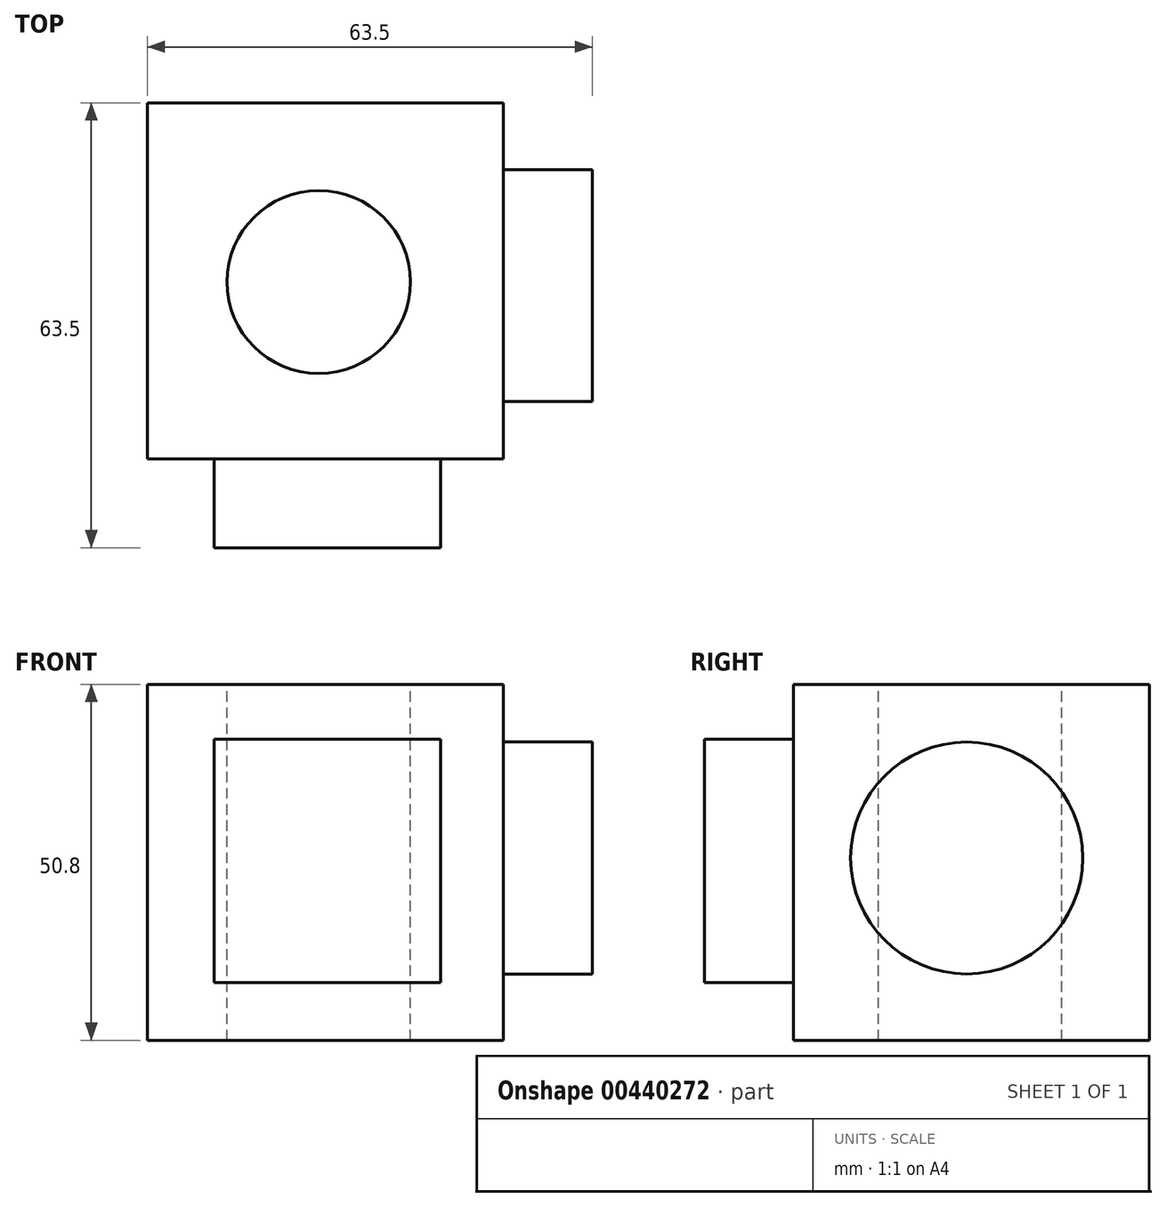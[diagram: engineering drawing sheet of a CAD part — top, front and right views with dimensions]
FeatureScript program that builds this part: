
annotation { "Feature Type Name" : "Feature", "Feature Type Description" : "" }
export const myFeature = defineFeature(function(context is Context, id is Id, definition is map)
    precondition{}
    {
        {
            var Q0;
            Q0=qCreatedBy(makeId("Front.planeOp"),FACE);
            var sketch = newSketch(context, id + "F0", { "sketchPlane" : qUnion([Q0])});
            skLineSegment(sketch, "E0.bottom", {"start": v(0, 0) * mm, "end": v(-50.8, 0) * mm});
            skLineSegment(sketch, "E0.top", {"start": v(0, 50.8) * mm, "end": v(-50.8, 50.8) * mm});
            skLineSegment(sketch, "E0.left", {"start": v(0, 0) * mm, "end": v(0, 50.8) * mm});
            skLineSegment(sketch, "E0.right", {"start": v(-50.8, 0) * mm, "end": v(-50.8, 50.8) * mm});
            skSolve(sketch);
        }
        {
            var Q0;
            Q0 = qSketchRegion(id + "F0", true);
            extrude(context, id + "F1", {"entities" : qUnion([Q0]), "depth" : 50.8 * mm});
        }
        {
            var Q0;
            Q0=makeQuery(id+"F1.opExtrude","SWEPT_FACE",FACE,{"disambiguationData":[OSD([sQuery(id+"F0.wireOp",EDGE,"E0.top")])]});
            var sketch = newSketch(context, id + "F2", { "sketchPlane" : qUnion([Q0])});
            skCircle(sketch, "E1", {"center": v(-26.35, -25.59) * mm, "radius": 13.07 * mm});
            skSolve(sketch);
        }
        {
            var Q0;
            Q0=makeQuery(id+"F2.imprint","IMPRINT",FACE,{"disambiguationData":[TD([[makeQuery(id+"F2.imprint","IMPRINT",EDGE,{"derivedFrom":sQuery(id+"F2.wireOp",EDGE,"E1")}),1.0]])]});
            extrude(context, id + "F3", {"entities" : qUnion([Q0]), "operationType" : NewBodyOperationType.REMOVE, "oppositeDirection" : true, "depth" : 50.8 * mm});
        }
        {
            var Q0;
            Q0=makeQuery(id+"F1.opExtrude","SWEPT_FACE",FACE,{"disambiguationData":[OSD([sQuery(id+"F0.wireOp",EDGE,"E0.left")])]});
            var sketch = newSketch(context, id + "F4", { "sketchPlane" : qUnion([Q0])});
            skCircle(sketch, "E2", {"center": v(-26.09, 26) * mm, "radius": 16.56 * mm});
            skSolve(sketch);
        }
        {
            var Q0;
            Q0 = qSketchRegion(id + "F4", true);
            extrude(context, id + "F5", {"entities" : qUnion([Q0]), "operationType" : NewBodyOperationType.ADD, "depth" : 12.7 * mm});
        }
        {
            var Q0;
            Q0=makeQuery(id+"F1.opExtrude","CAP_FACE",FACE,{"disambiguationData":[OSD([sQuery(id+"F0.wireOp",EDGE,"E0.bottom"),sQuery(id+"F0.wireOp",EDGE,"E0.top"),sQuery(id+"F0.wireOp",EDGE,"E0.left"),sQuery(id+"F0.wireOp",EDGE,"E0.right")])],"isStart":false});
            var sketch = newSketch(context, id + "F6", { "sketchPlane" : qUnion([Q0])});
            skLineSegment(sketch, "E3.bottom", {"start": v(-41.25, 42.96) * mm, "end": v(-8.97, 42.96) * mm});
            skLineSegment(sketch, "E3.top", {"start": v(-41.25, 8.21) * mm, "end": v(-8.97, 8.21) * mm});
            skLineSegment(sketch, "E3.left", {"start": v(-41.25, 42.96) * mm, "end": v(-41.25, 8.21) * mm});
            skLineSegment(sketch, "E3.right", {"start": v(-8.97, 42.96) * mm, "end": v(-8.97, 8.21) * mm});
            skSolve(sketch);
        }
        {
            var Q0;
            Q0=makeQuery(id+"F6.imprint","IMPRINT",FACE,{"disambiguationData":[TD([[makeQuery(id+"F6.imprint","IMPRINT",EDGE,{"derivedFrom":sQuery(id+"F6.wireOp",EDGE,"E3.bottom")}),-1.0]])]});
            extrude(context, id + "F7", {"entities" : qUnion([Q0]), "operationType" : NewBodyOperationType.ADD, "depth" : 12.7 * mm});
        }
    });
